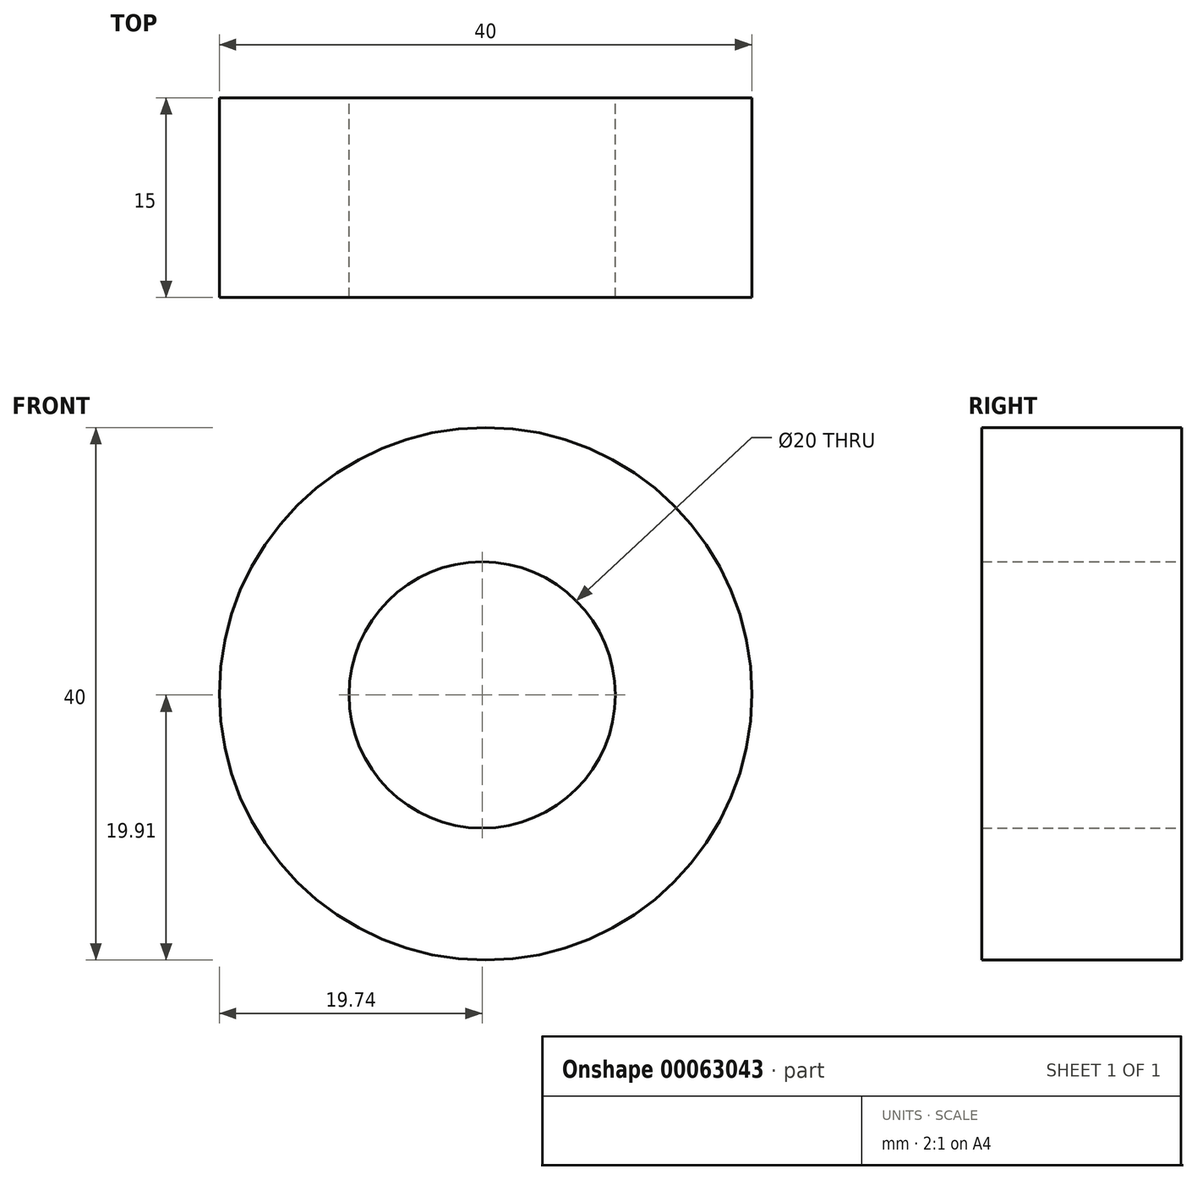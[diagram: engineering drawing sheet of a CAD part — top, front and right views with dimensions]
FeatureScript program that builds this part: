
annotation { "Feature Type Name" : "Feature", "Feature Type Description" : "" }
export const myFeature = defineFeature(function(context is Context, id is Id, definition is map)
    precondition{}
    {
        {
            var Q0;
            Q0=qCreatedBy(makeId("Front.planeOp"),FACE);
            var sketch = newSketch(context, id + "F0", { "sketchPlane" : qUnion([Q0])});
            skCircle(sketch, "E0", {"center": v(0, 0) * mm, "radius": 10 * mm});
            skCircle(sketch, "E1", {"center": v(0.26, 0.09) * mm, "radius": 20 * mm});
            skSolve(sketch);
        }
        {
            var Q0;
            Q0=makeQuery(id+"F0.imprint","IMPRINT",FACE,{"disambiguationData":[TD([[makeQuery(id+"F0.imprint","IMPRINT",EDGE,{"derivedFrom":sQuery(id+"F0.wireOp",EDGE,"E0")}),-1.0]])]});
            extrude(context, id + "F1", {"entities" : qUnion([Q0]), "depth" : 15 * mm});
        }
    });
